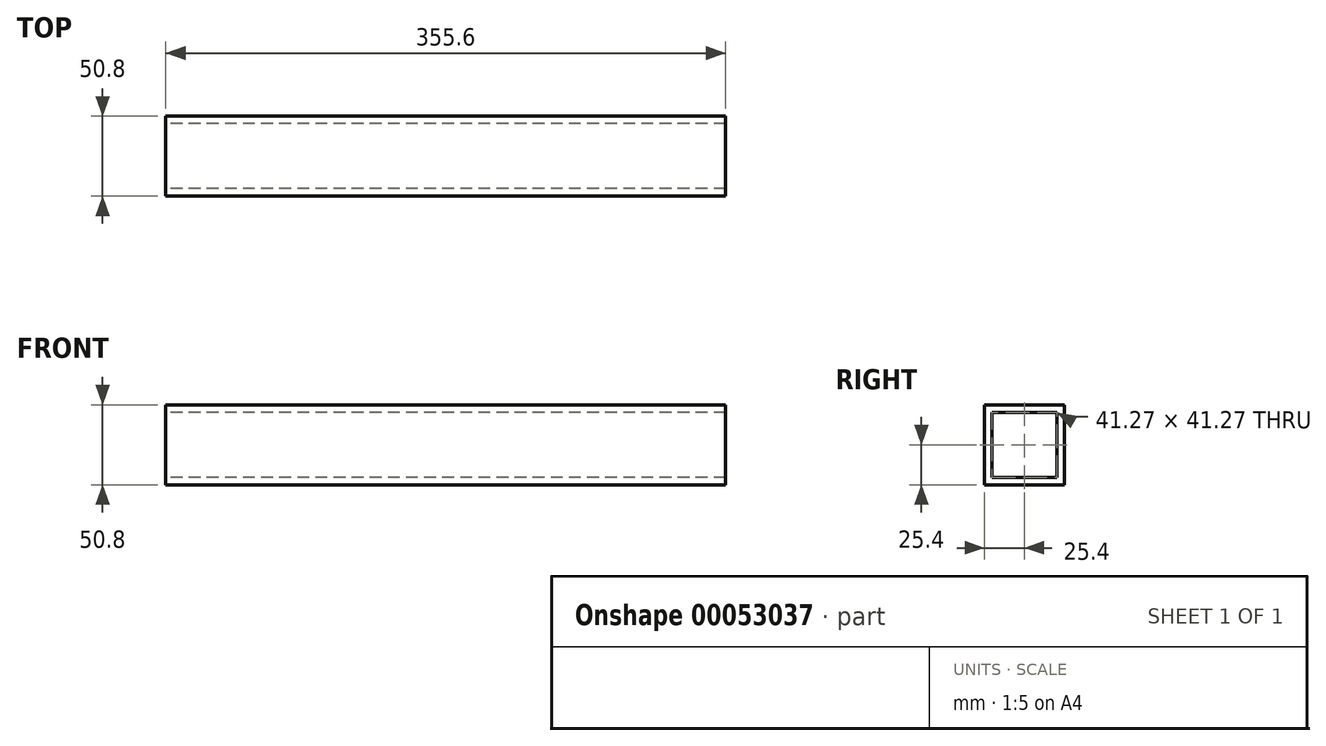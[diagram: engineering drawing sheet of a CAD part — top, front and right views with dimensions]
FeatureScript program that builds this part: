
annotation { "Feature Type Name" : "Feature", "Feature Type Description" : "" }
export const myFeature = defineFeature(function(context is Context, id is Id, definition is map)
    precondition{}
    {
        {
            var Q0;
            Q0=qCreatedBy(makeId("Right.planeOp"),FACE);
            var sketch = newSketch(context, id + "F0", { "sketchPlane" : qUnion([Q0])});
            skLineSegment(sketch, "E0.bottom", {"start": v(0, 0) * mm, "end": v(-50.8, 0) * mm});
            skLineSegment(sketch, "E0.top", {"start": v(0, 50.8) * mm, "end": v(-50.8, 50.8) * mm});
            skLineSegment(sketch, "E0.left", {"start": v(0, 0) * mm, "end": v(0, 50.8) * mm});
            skLineSegment(sketch, "E0.right", {"start": v(-50.8, 0) * mm, "end": v(-50.8, 50.8) * mm});
            skLineSegment(sketch, "E1.bottom", {"start": v(-46.04, 46.04) * mm, "end": v(-4.76, 46.04) * mm});
            skLineSegment(sketch, "E1.top", {"start": v(-46.04, 4.76) * mm, "end": v(-4.76, 4.76) * mm});
            skLineSegment(sketch, "E1.left", {"start": v(-46.04, 46.04) * mm, "end": v(-46.04, 4.76) * mm});
            skLineSegment(sketch, "E1.right", {"start": v(-4.76, 46.04) * mm, "end": v(-4.76, 4.76) * mm});
            skSolve(sketch);
        }
        {
            var Q0;
            Q0=makeQuery(id+"F0.imprint","IMPRINT",FACE,{"disambiguationData":[TD([[makeQuery(id+"F0.imprint","IMPRINT",EDGE,{"derivedFrom":sQuery(id+"F0.wireOp",EDGE,"E0.bottom")}),-1.0]])]});
            extrude(context, id + "F1", {"entities" : qUnion([Q0]), "depth" : 355.6 * mm});
        }
    });
